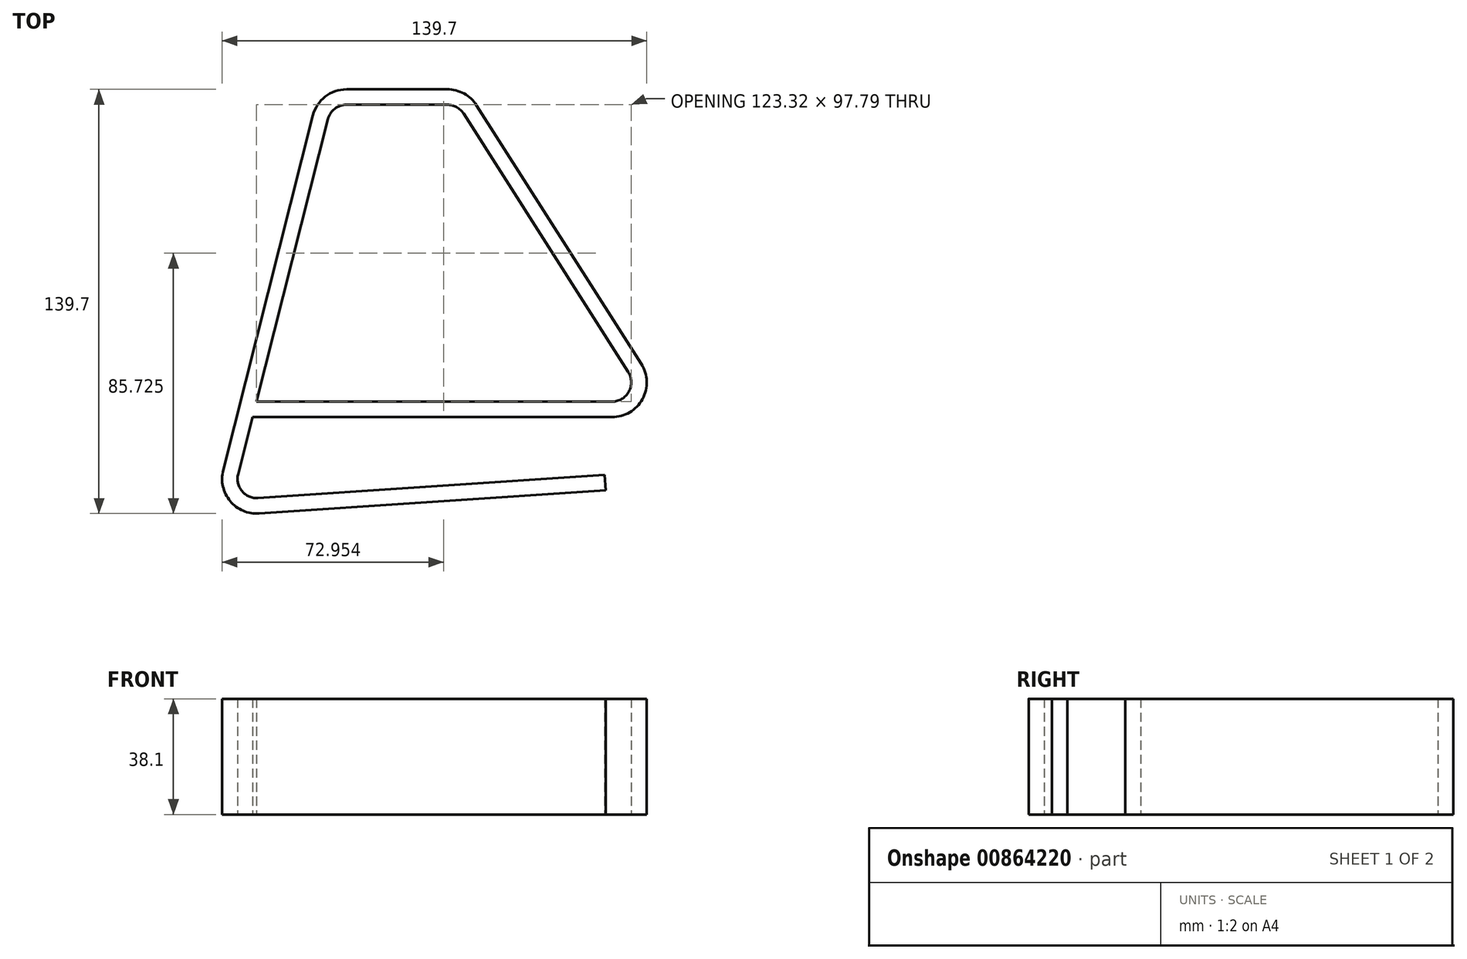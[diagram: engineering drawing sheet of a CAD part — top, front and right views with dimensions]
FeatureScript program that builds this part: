
annotation { "Feature Type Name" : "Feature", "Feature Type Description" : "" }
export const myFeature = defineFeature(function(context is Context, id is Id, definition is map)
    precondition{}
    {
        {
            var Q0;
            Q0=qCreatedBy(makeId("Top.planeOp"),FACE);
            var sketch = newSketch(context, id + "F0", { "sketchPlane" : qUnion([Q0])});
            skLineSegment(sketch, "E0", {"start": v(-76.5, 93) * mm, "end": v(-106.04, -23.84) * mm});
            skLineSegment(sketch, "E1", {"start": v(-99.46, -31.74) * mm, "end": v(14.58, -24.13) * mm});
            skLineSegment(sketch, "E2", {"start": v(-70.35, 97.79) * mm, "end": v(-37.22, 97.79) * mm});
            skLineSegment(sketch, "E3", {"start": v(-31.86, 94.85) * mm, "end": v(22.31, 9.76) * mm});
            skLineSegment(sketch, "E4", {"start": v(16.96, 0) * mm, "end": v(0, 0) * mm});
            skPoint(sketch, "E5.visualSharp", {"position": v(-33.73, 97.79) * mm});
            skArc(sketch, "E5.filletArc", {"start": v(-31.86, 94.85) * mm, "mid": v(-34.16, 97) * mm, "end": v(-37.22, 97.8) * mm});
            skPoint(sketch, "E6.visualSharp", {"position": v(-75.3, 97.79) * mm});
            skArc(sketch, "E6.filletArc", {"start": v(-70.35, 97.8) * mm, "mid": v(-74.25, 96.45) * mm, "end": v(-76.5, 93) * mm});
            skPoint(sketch, "E7.visualSharp", {"position": v(28.53, 0) * mm});
            skArc(sketch, "E7.filletArc", {"start": v(16.96, 0) * mm, "mid": v(22.52, 3.3) * mm, "end": v(22.31, 9.76) * mm});
            skPoint(sketch, "E8.visualSharp", {"position": v(-108.18, -32.32) * mm});
            skArc(sketch, "E8.filletArc", {"start": v(-106.04, -23.84) * mm, "mid": v(-104.76, -29.47) * mm, "end": v(-99.46, -31.74) * mm});
            skLineSegment(sketch, "E9.0", {"start": v(-99.12, -36.8) * mm, "end": v(14.92, -29.2) * mm});
            skArc(sketch, "E9.1", {"start": v(-110.97, -22.6) * mm, "mid": v(-108.66, -32.72) * mm, "end": v(-99.12, -36.8) * mm});
            skLineSegment(sketch, "E9.2", {"start": v(-81.43, 94.24) * mm, "end": v(-110.97, -22.6) * mm});
            skArc(sketch, "E9.3", {"start": v(-70.35, 102.87) * mm, "mid": v(-77.38, 100.46) * mm, "end": v(-81.43, 94.24) * mm});
            skArc(sketch, "E9.4", {"start": v(16.96, -5.08) * mm, "mid": v(26.98, 0.85) * mm, "end": v(26.6, 12.49) * mm});
            skLineSegment(sketch, "E9.5", {"start": v(-27.58, 97.58) * mm, "end": v(26.6, 12.49) * mm});
            skArc(sketch, "E9.6", {"start": v(-27.58, 97.58) * mm, "mid": v(-31.72, 101.46) * mm, "end": v(-37.22, 102.87) * mm});
            skLineSegment(sketch, "E9.7", {"start": v(-70.35, 102.87) * mm, "end": v(-37.22, 102.87) * mm});
            skLineSegment(sketch, "E10", {"start": v(14.92, -29.2) * mm, "end": v(14.58, -24.13) * mm});
            skLineSegment(sketch, "E11", {"start": v(16.96, 0) * mm, "end": v(16.96, -5.08) * mm});
            skLineSegment(sketch, "E12.0", {"start": v(60.62, -5.08) * mm, "end": v(0, -5.08) * mm});
            skLineSegment(sketch, "E13", {"start": v(0, -5.08) * mm, "end": v(-101.3, -5.08) * mm});
            skLineSegment(sketch, "E14", {"start": v(-111.31, -16.37) * mm, "end": v(-111.31, -35.48) * mm});
            skPoint(sketch, "E15", {"position": v(-111.31, -25.4) * mm});
            skLineSegment(sketch, "E16", {"start": v(28.39, 28.24) * mm, "end": v(28.39, 0) * mm});
            skPoint(sketch, "E17", {"position": v(28.39, 6.35) * mm});
            skLineSegment(sketch, "E18", {"start": v(-89.6, -36.83) * mm, "end": v(-108.15, -36.83) * mm});
            skPoint(sketch, "E19", {"position": v(-99.88, -36.83) * mm});
            skPoint(sketch, "E20", {"position": v(-100.01, 0) * mm});
            skLineSegment(sketch, "E21", {"start": v(-100.01, 0) * mm, "end": v(4.03, 0) * mm});
            skLineSegment(sketch, "E22", {"start": v(-92.55, -31.75) * mm, "end": v(-101.7, -31.75) * mm});
            skLineSegment(sketch, "E23", {"start": v(-101.7, -31.75) * mm, "end": v(-98.69, -31.75) * mm});
            skPoint(sketch, "E24", {"position": v(-99.88, -31.75) * mm});
            skSolve(sketch);
        }
        {
            var Q0;
            Q0=makeQuery(id+"F0.imprint","IMPRINT",FACE,{"disambiguationData":[TD([[makeQuery(id+"F0.imprint","IMPRINT",EDGE,{"derivedFrom":sQuery(id+"F0.wireOp",EDGE,"E1")}),-1.0]])]});
            var Q1;
            {var subQ0=sQuery(id+"F0.wireOp",EDGE,"E11");Q1=makeQuery(id+"F0.imprint","IMPRINT",FACE,{"disambiguationData":[TD([[makeQuery(id+"F0.imprint","IMPRINT",EDGE,{"derivedFrom":subQ0}),-1.0]])]});}
            extrude(context, id + "F1", {"entities" : qUnion([Q0, Q1]), "depth" : 38.1 * mm, "offsetDistance" : 25.4 * mm});
        }
    });
